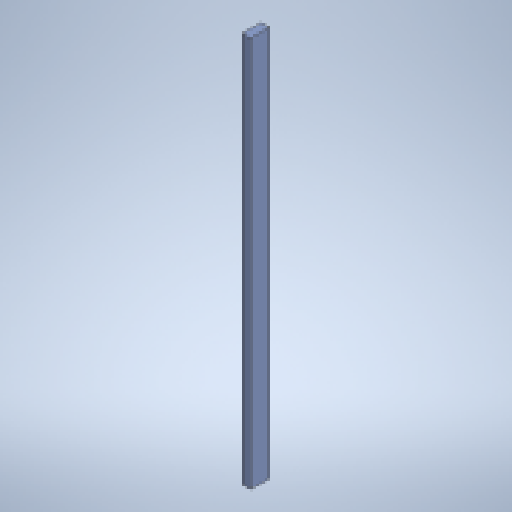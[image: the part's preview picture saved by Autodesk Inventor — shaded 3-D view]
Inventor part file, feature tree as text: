
AUTODESK INVENTOR PART (.ipt)
format: ipt  version: 2025.1 (Build 291241020, 241B)  size: 137,728 bytes
history: native  units: in
note: dims shown in document units (in); Inventor stores cm internally (conversion verified against a paired STEP export)
features: extrude x1, sketch x1, other x1
ambient origin geometry x8: Origin, YZ Plane, XZ Plane, XY Plane, X Axis, Y Axis, Z Axis, Center Point
bodies: Solid1 (feature_tree)
feature tree (3):
  extrude  "Extrusion1"  Depth=1.5in
  sketch  "Sketch1"  dims[d0=3.5in d1=1.5in d2=72.0in d3=0.0in]
  other  "Finish1"
